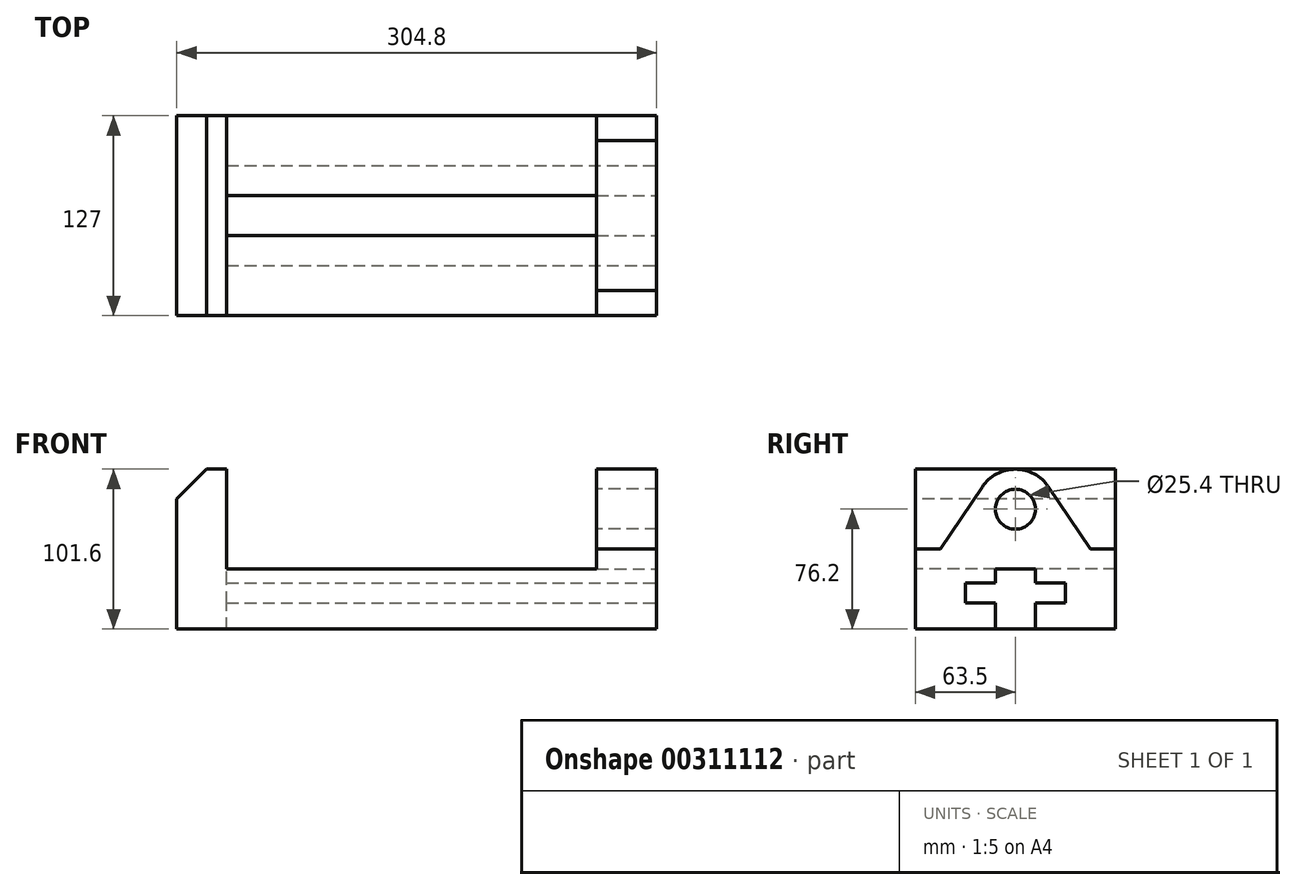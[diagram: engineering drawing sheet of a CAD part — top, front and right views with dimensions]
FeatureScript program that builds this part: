
annotation { "Feature Type Name" : "Feature", "Feature Type Description" : "" }
export const myFeature = defineFeature(function(context is Context, id is Id, definition is map)
    precondition{}
    {
        {
            var Q0;
            Q0=qCreatedBy(makeId("Right.planeOp"),FACE);
            var sketch = newSketch(context, id + "F0", { "sketchPlane" : qUnion([Q0])});
            skLineSegment(sketch, "E0", {"start": v(0, 0) * mm, "end": v(127, 0) * mm});
            skLineSegment(sketch, "E1", {"start": v(127, 0) * mm, "end": v(127, 50.8) * mm});
            skLineSegment(sketch, "E2", {"start": v(0, 0) * mm, "end": v(0, 50.8) * mm});
            skLineSegment(sketch, "E3", {"start": v(0, 50.8) * mm, "end": v(15.88, 50.8) * mm});
            skLineSegment(sketch, "E4", {"start": v(127, 50.8) * mm, "end": v(111.12, 50.8) * mm});
            skLineSegment(sketch, "E5", {"start": v(111.13, 50.8) * mm, "end": v(84.6, 90.35) * mm});
            skLineSegment(sketch, "E6", {"start": v(15.88, 50.8) * mm, "end": v(42.4, 90.35) * mm});
            skArc(sketch, "E7", {"start": v(84.6, 90.35) * mm, "mid": v(63.5, 101.6) * mm, "end": v(42.4, 90.35) * mm});
            skCircle(sketch, "E8", {"center": v(63.5, 76.2) * mm, "radius": 12.7 * mm});
            skPoint(sketch, "E9.start.orphan", {"position": v(63.5, 0) * mm});
            skSolve(sketch);
        }
        {
            var Q0;
            Q0 = qSketchRegion(id + "F0", true);
            extrude(context, id + "F1", {"entities" : qUnion([Q0]), "depth" : 38.1 * mm});
        }
        {
            var Q0;
            Q0=qCreatedBy(makeId("Front.planeOp"),FACE);
            var sketch = newSketch(context, id + "F2", { "sketchPlane" : qUnion([Q0])});
            skLineSegment(sketch, "E10", {"start": v(0, 0) * mm, "end": v(-266.7, 0) * mm});
            skLineSegment(sketch, "E11", {"start": v(-266.7, 0) * mm, "end": v(-266.7, 38.1) * mm});
            skLineSegment(sketch, "E12", {"start": v(0, 38.1) * mm, "end": v(0, 0) * mm});
            skLineSegment(sketch, "E13", {"start": v(-266.7, 0) * mm, "end": v(-266.7, 82.55) * mm});
            skLineSegment(sketch, "E14", {"start": v(-247.65, 101.6) * mm, "end": v(-266.7, 82.55) * mm});
            skLineSegment(sketch, "E15", {"start": v(-247.65, 101.6) * mm, "end": v(-234.95, 101.6) * mm});
            skLineSegment(sketch, "E16", {"start": v(-234.95, 101.6) * mm, "end": v(-234.95, 38.1) * mm});
            skLineSegment(sketch, "E17", {"start": v(-234.95, 38.1) * mm, "end": v(0, 38.1) * mm});
            skSolve(sketch);
        }
        {
            var Q0;
            Q0 = qSketchRegion(id + "F2", true);
            extrude(context, id + "F3", {"entities" : qUnion([Q0]), "operationType" : NewBodyOperationType.ADD, "oppositeDirection" : true, "depth" : 127 * mm});
        }
        {
            var Q0;
            Q0=makeQuery(id+"F1.opExtrude","CAP_FACE",FACE,{"disambiguationData":[OSD([sQuery(id+"F0.wireOp",EDGE,"E0"),sQuery(id+"F0.wireOp",EDGE,"E1"),sQuery(id+"F0.wireOp",EDGE,"E2"),sQuery(id+"F0.wireOp",EDGE,"E3"),sQuery(id+"F0.wireOp",EDGE,"E4"),sQuery(id+"F0.wireOp",EDGE,"E5"),sQuery(id+"F0.wireOp",EDGE,"E6"),sQuery(id+"F0.wireOp",EDGE,"E7"),sQuery(id+"F0.wireOp",EDGE,"E8")])],"isStart":false});
            var sketch = newSketch(context, id + "F4", { "sketchPlane" : qUnion([Q0])});
            skLineSegment(sketch, "E18", {"start": v(0, 0) * mm, "end": v(50.8, 0) * mm});
            skLineSegment(sketch, "E19", {"start": v(50.8, 0) * mm, "end": v(50.8, 16.51) * mm});
            skLineSegment(sketch, "E20", {"start": v(50.8, 16.51) * mm, "end": v(31.75, 16.51) * mm});
            skLineSegment(sketch, "E21", {"start": v(31.75, 16.51) * mm, "end": v(31.75, 29.21) * mm});
            skLineSegment(sketch, "E22", {"start": v(31.75, 29.21) * mm, "end": v(50.8, 29.21) * mm});
            skLineSegment(sketch, "E23", {"start": v(50.8, 29.21) * mm, "end": v(50.8, 38.1) * mm});
            skLineSegment(sketch, "E24", {"start": v(50.8, 38.1) * mm, "end": v(76.2, 38.1) * mm});
            skLineSegment(sketch, "E25", {"start": v(76.2, 38.1) * mm, "end": v(76.2, 29.21) * mm});
            skLineSegment(sketch, "E26", {"start": v(76.2, 29.21) * mm, "end": v(95.25, 29.21) * mm});
            skLineSegment(sketch, "E27", {"start": v(95.25, 29.21) * mm, "end": v(95.25, 16.51) * mm});
            skLineSegment(sketch, "E28", {"start": v(95.25, 16.51) * mm, "end": v(76.2, 16.51) * mm});
            skLineSegment(sketch, "E29", {"start": v(76.2, 16.51) * mm, "end": v(76.2, 0) * mm});
            skLineSegment(sketch, "E30", {"start": v(76.2, 0) * mm, "end": v(50.8, 0) * mm});
            skSolve(sketch);
        }
        {
            var Q0;
            Q0 = qSketchRegion(id + "F4", true);
            extrude(context, id + "F5", {"entities" : qUnion([Q0]), "operationType" : NewBodyOperationType.REMOVE, "oppositeDirection" : true, "depth" : 273.05 * mm});
        }
    });
